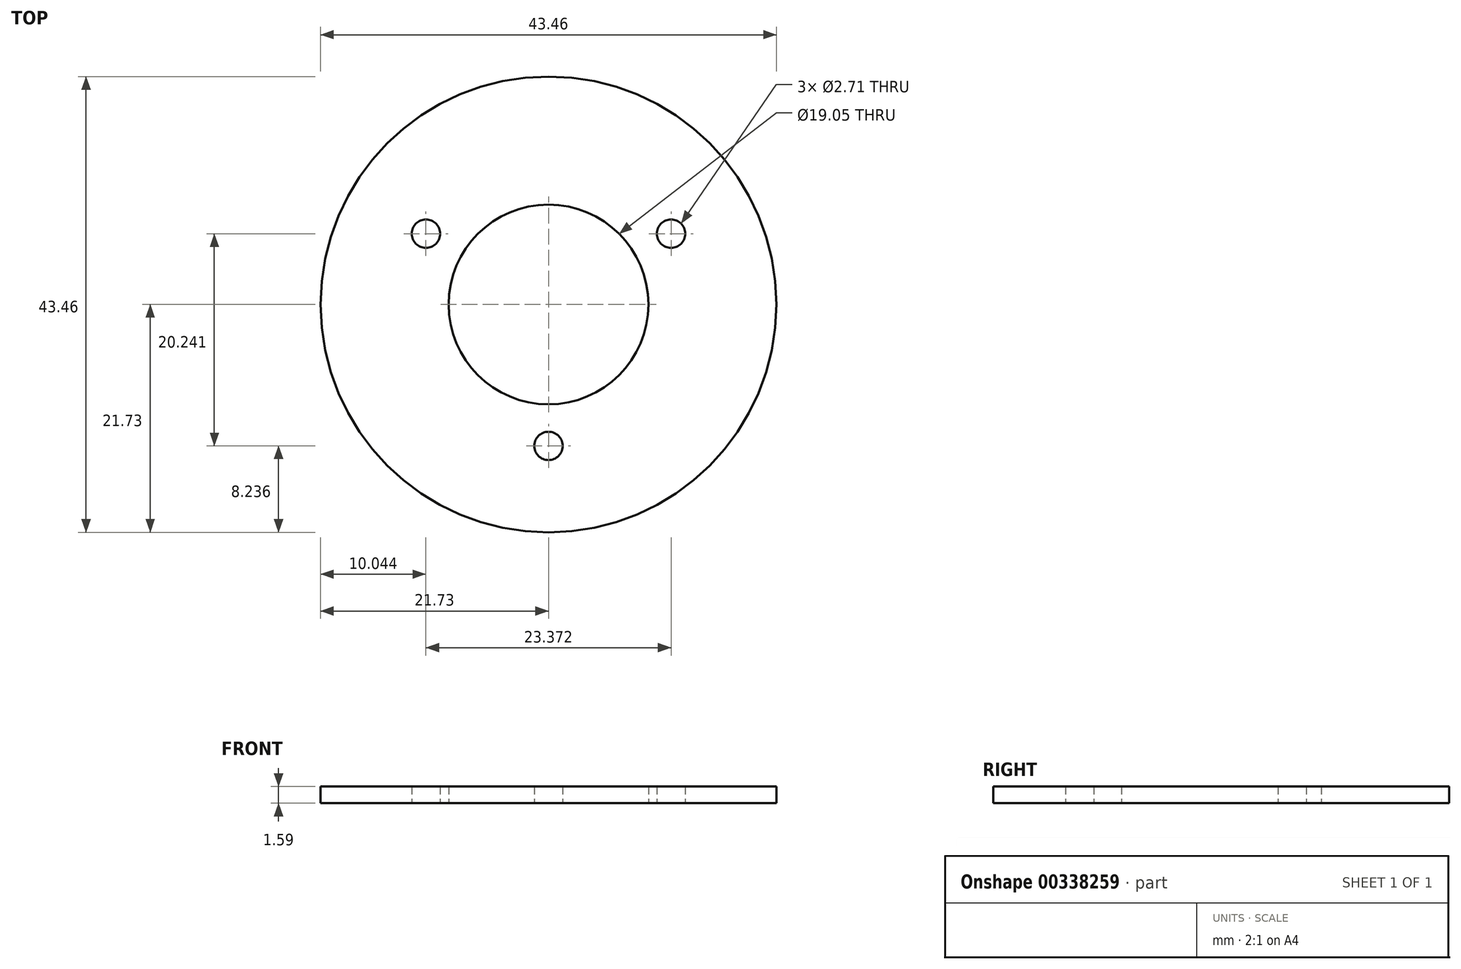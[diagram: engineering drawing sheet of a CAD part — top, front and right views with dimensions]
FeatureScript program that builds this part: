
annotation { "Feature Type Name" : "Feature", "Feature Type Description" : "" }
export const myFeature = defineFeature(function(context is Context, id is Id, definition is map)
    precondition{}
    {
        {
            var Q0;
            Q0=qCreatedBy(makeId("Top.planeOp"),FACE);
            var sketch = newSketch(context, id + "F0", { "sketchPlane" : qUnion([Q0])});
            skCircle(sketch, "E0", {"center": v(0, 0) * mm, "radius": 9.52 * mm});
            skCircle(sketch, "E1", {"center": v(0, 0) * mm, "radius": 21.73 * mm});
            skLineSegment(sketch, "E2", {"start": v(0, 0) * mm, "end": v(0, -13.5) * mm, "construction": true});
            skLineSegment(sketch, "E3", {"start": v(0, -13.5) * mm, "end": v(11.69, 6.75) * mm, "construction": true});
            skLineSegment(sketch, "E4", {"start": v(11.69, 6.75) * mm, "end": v(0, 0) * mm, "construction": true});
            skLineSegment(sketch, "E5", {"start": v(0, 0) * mm, "end": v(-11.69, 6.75) * mm, "construction": true});
            skLineSegment(sketch, "E6", {"start": v(-11.69, 6.75) * mm, "end": v(0, -13.5) * mm, "construction": true});
            skLineSegment(sketch, "E7", {"start": v(-11.69, 6.75) * mm, "end": v(11.69, 6.75) * mm, "construction": true});
            skCircle(sketch, "E8", {"center": v(0, -13.5) * mm, "radius": 3.97 * mm, "construction": true});
            skCircle(sketch, "E9", {"center": v(-11.69, 6.75) * mm, "radius": 1.35 * mm});
            skCircle(sketch, "E10", {"center": v(11.69, 6.75) * mm, "radius": 1.35 * mm});
            skCircle(sketch, "E11", {"center": v(0, -13.5) * mm, "radius": 1.35 * mm});
            skSolve(sketch);
        }
        {
            var Q0;
            Q0=qSketchRegion(id+"F0",true);
            extrude(context, id + "F1", {"entities" : qUnion([Q0]), "depth" : 1.59 * mm});
        }
    });
